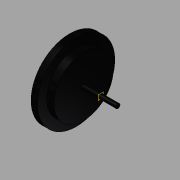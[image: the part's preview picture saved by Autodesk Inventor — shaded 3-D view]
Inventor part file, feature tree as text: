
AUTODESK INVENTOR PART (.ipt)
format: ipt  version: 2015 (Build 190159000, 159)  size: 140,800 bytes
history: native  units: in
note: dims shown in document units (in); Inventor stores cm internally (conversion verified against a paired STEP export)
features: sketch x5, other x3, plane x1
ambient origin geometry x8: Origin, YZ Plane, XZ Plane, XY Plane, X Axis, Y Axis, Z Axis, Center Point
bodies: Solid1 (feature_tree)
feature tree (9):
  other  "rueda.ipt"
  other  "Solid1::rueda.ipt"
  other  "TaggingFeature1"
  sketch  "Sketch2"  dims[d0=0.3937in]
  sketch  "Sketch3"
  sketch  "Sketch7"
  sketch  "Sketch12"
  sketch  "Sketch13"
  plane  "Work Plane1"
